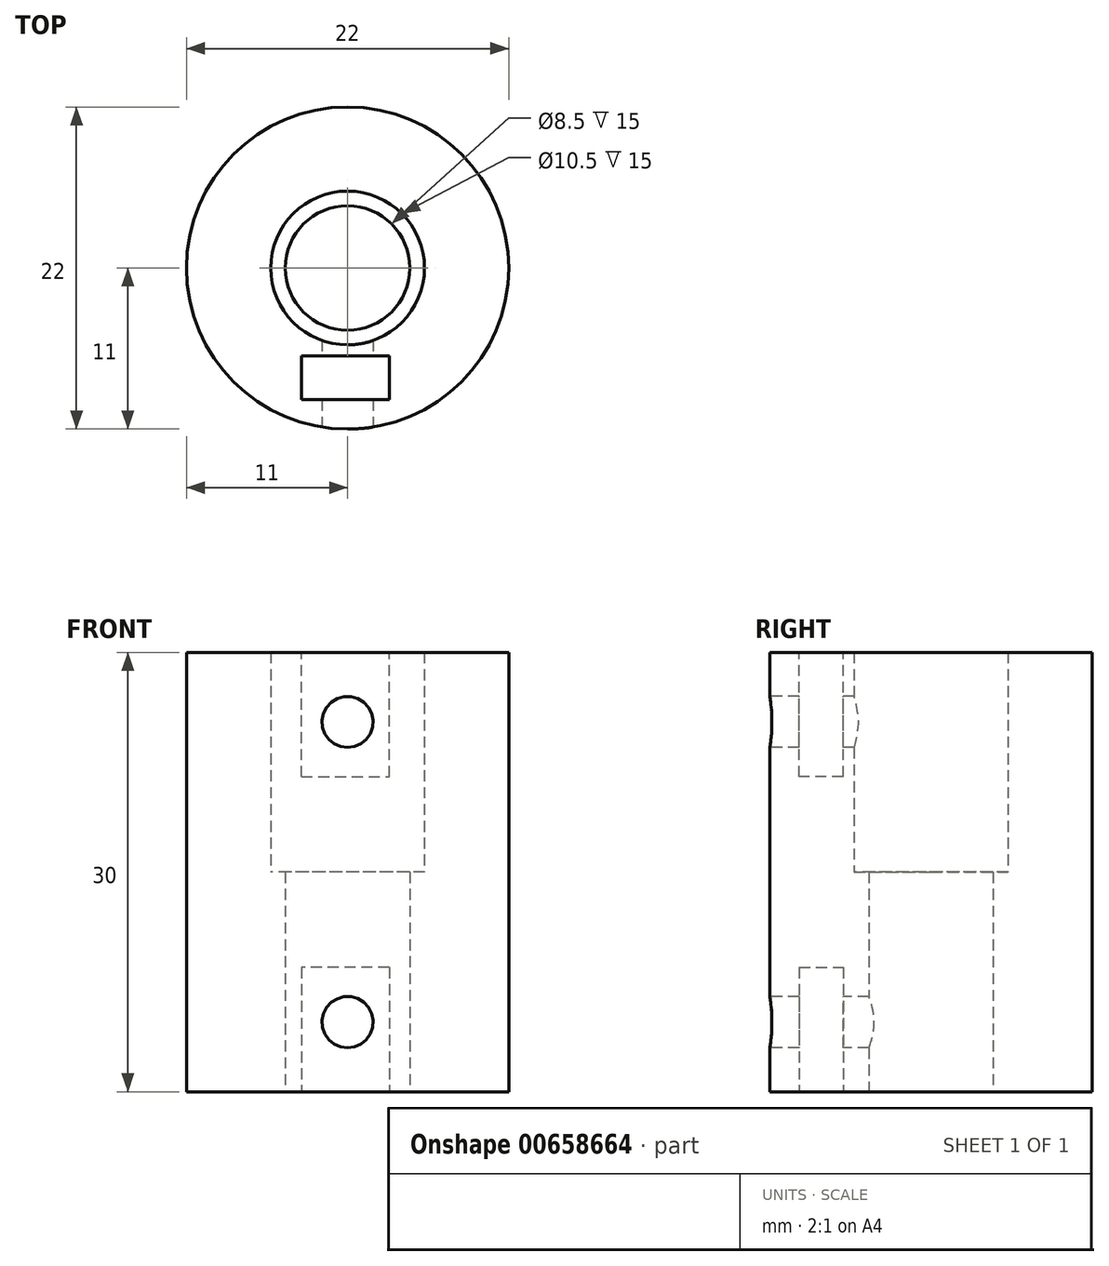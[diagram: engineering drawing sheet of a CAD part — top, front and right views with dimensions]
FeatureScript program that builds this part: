
annotation { "Feature Type Name" : "Feature", "Feature Type Description" : "" }
export const myFeature = defineFeature(function(context is Context, id is Id, definition is map)
    precondition{}
    {
        {
            var Q0;
            Q0=qCreatedBy(makeId("Top.planeOp"),FACE);
            var sketch = newSketch(context, id + "F0", { "sketchPlane" : qUnion([Q0])});
            skCircle(sketch, "E0", {"center": v(0, 0) * mm, "radius": 11 * mm});
            skCircle(sketch, "E1", {"center": v(0, 0) * mm, "radius": 4.25 * mm});
            skSolve(sketch);
        }
        {
            var Q0;
            Q0=makeQuery(id+"F0.imprint","IMPRINT",FACE,{"disambiguationData":[TD([[makeQuery(id+"F0.imprint","IMPRINT",EDGE,{"derivedFrom":sQuery(id+"F0.wireOp",EDGE,"E0")}),1.0]])]});
            extrude(context, id + "F1", {"entities" : qUnion([Q0]), "depth" : 15 * mm});
        }
        {
            var Q0;
            Q0=makeQuery(id+"F1.opExtrude","CAP_FACE",FACE,{"disambiguationData":[OSD([sQuery(id+"F0.wireOp",EDGE,"E0"),sQuery(id+"F0.wireOp",EDGE,"E1")])],"isStart":false});
            var sketch = newSketch(context, id + "F2", { "sketchPlane" : qUnion([Q0])});
            skCircle(sketch, "E2", {"center": v(0, 0) * mm, "radius": 11 * mm});
            skCircle(sketch, "E3", {"center": v(0, 0) * mm, "radius": 5.25 * mm});
            skSolve(sketch);
        }
        {
            var Q0;
            Q0=makeQuery(id+"F2.imprint","IMPRINT",FACE,{"disambiguationData":[TD([[makeQuery(id+"F2.imprint","IMPRINT",EDGE,{"derivedFrom":sQuery(id+"F2.wireOp",EDGE,"E2")}),1.0]])]});
            extrude(context, id + "F3", {"entities" : qUnion([Q0]), "operationType" : NewBodyOperationType.ADD, "depth" : 15 * mm});
        }
        {
            var Q0;
            Q0=makeQuery(id+"F3.opExtrude","CAP_FACE",FACE,{"disambiguationData":[OSD([sQuery(id+"F2.wireOp",EDGE,"E2"),sQuery(id+"F2.wireOp",EDGE,"E3")])],"isStart":false});
            var sketch = newSketch(context, id + "F4", { "sketchPlane" : qUnion([Q0])});
            skLineSegment(sketch, "E4.bottom", {"start": v(-3.15, -6) * mm, "end": v(2.85, -6) * mm});
            skLineSegment(sketch, "E4.top", {"start": v(-3.15, -9) * mm, "end": v(2.85, -9) * mm});
            skLineSegment(sketch, "E4.left", {"start": v(-3.15, -6) * mm, "end": v(-3.15, -9) * mm});
            skLineSegment(sketch, "E4.right", {"start": v(2.85, -6) * mm, "end": v(2.85, -9) * mm});
            skSolve(sketch);
        }
        {
            var Q0;
            Q0=makeQuery(id+"F4.imprint","IMPRINT",FACE,{"disambiguationData":[TD([[makeQuery(id+"F4.imprint","IMPRINT",EDGE,{"derivedFrom":sQuery(id+"F4.wireOp",EDGE,"E4.bottom")}),-1.0]])]});
            extrude(context, id + "F5", {"entities" : qUnion([Q0]), "operationType" : NewBodyOperationType.REMOVE, "oppositeDirection" : true, "depth" : 8.5 * mm});
        }
        {
            var Q0;
            Q0=makeQuery(id+"F5.boolean.opBoolean","COPY",FACE,{"derivedFrom":makeQuery(id+"F5.opExtrude","SWEPT_FACE",FACE,{"disambiguationData":[OSD([sQuery(id+"F4.wireOp",EDGE,"E4.bottom")])]})});
            var sketch = newSketch(context, id + "F6", { "sketchPlane" : qUnion([Q0])});
            skCircle(sketch, "E5", {"center": v(0, 25.25) * mm, "radius": 1.75 * mm});
            skLineSegment(sketch, "E6.0.0", {"start": v(2.85, 30) * mm, "end": v(-3.15, 30) * mm});
            skLineSegment(sketch, "E6.0.1", {"start": v(-3.15, 30) * mm, "end": v(-3.15, 21.5) * mm});
            skLineSegment(sketch, "E6.0.2", {"start": v(-3.15, 21.5) * mm, "end": v(2.85, 21.5) * mm});
            skLineSegment(sketch, "E6.0.3", {"start": v(2.85, 21.5) * mm, "end": v(2.85, 30) * mm});
            skSolve(sketch);
        }
        {
            var Q0;
            Q0=makeQuery(id+"F6.imprint","IMPRINT",FACE,{"disambiguationData":[TD([[makeQuery(id+"F6.imprint","IMPRINT",EDGE,{"derivedFrom":sQuery(id+"F6.wireOp",EDGE,"E5")}),1.0]])]});
            extrude(context, id + "F7", {"entities" : qUnion([Q0]), "operationType" : NewBodyOperationType.REMOVE, "oppositeDirection" : true, "depth" : 10 * mm, "symmetric" : true});
        }
        {
            var Q0;
            Q0=makeQuery(id+"F1.opExtrude","CAP_FACE",FACE,{"disambiguationData":[OSD([sQuery(id+"F0.wireOp",EDGE,"E0"),sQuery(id+"F0.wireOp",EDGE,"E1")])],"isStart":true});
            var sketch = newSketch(context, id + "F8", { "sketchPlane" : qUnion([Q0])});
            skCircle(sketch, "E7.0.0", {"center": v(0, 0) * mm, "radius": 11 * mm});
            skLineSegment(sketch, "E8.0.0", {"start": v(2.85, 6) * mm, "end": v(-3.15, 6) * mm});
            skLineSegment(sketch, "E8.0.1", {"start": v(-3.15, 6) * mm, "end": v(-3.15, 9) * mm});
            skLineSegment(sketch, "E8.0.2", {"start": v(-3.15, 9) * mm, "end": v(2.85, 9) * mm});
            skLineSegment(sketch, "E8.0.3", {"start": v(2.85, 9) * mm, "end": v(2.85, 6) * mm});
            skSolve(sketch);
        }
        {
            var Q0;
            Q0=makeQuery(id+"F8.imprint","IMPRINT",FACE,{"disambiguationData":[TD([[makeQuery(id+"F8.imprint","IMPRINT",EDGE,{"derivedFrom":sQuery(id+"F8.wireOp",EDGE,"E8.0.0")}),-1.0]])]});
            extrude(context, id + "F9", {"entities" : qUnion([Q0]), "operationType" : NewBodyOperationType.REMOVE, "oppositeDirection" : true, "depth" : 8.5 * mm});
        }
        {
            var Q0;
            Q0=makeQuery(id+"F9.boolean.opBoolean","COPY",FACE,{"derivedFrom":makeQuery(id+"F9.opExtrude","SWEPT_FACE",FACE,{"disambiguationData":[OSD([sQuery(id+"F8.wireOp",EDGE,"E8.0.0")])]})});
            var sketch = newSketch(context, id + "F10", { "sketchPlane" : qUnion([Q0])});
            skLineSegment(sketch, "E9.0.0", {"start": v(-3.15, 0) * mm, "end": v(2.85, 0) * mm});
            skLineSegment(sketch, "E9.0.1", {"start": v(2.85, 0) * mm, "end": v(2.85, 8.5) * mm});
            skLineSegment(sketch, "E9.0.2", {"start": v(2.85, 8.5) * mm, "end": v(-3.15, 8.5) * mm});
            skLineSegment(sketch, "E9.0.3", {"start": v(-3.15, 8.5) * mm, "end": v(-3.15, 0) * mm});
            skCircle(sketch, "E10", {"center": v(0, 4.75) * mm, "radius": 1.75 * mm});
            skSolve(sketch);
        }
        {
            var Q0;
            Q0=makeQuery(id+"F10.imprint","IMPRINT",FACE,{"disambiguationData":[TD([[makeQuery(id+"F10.imprint","IMPRINT",EDGE,{"derivedFrom":sQuery(id+"F10.wireOp",EDGE,"E10")}),1.0]])]});
            extrude(context, id + "F11", {"entities" : qUnion([Q0]), "operationType" : NewBodyOperationType.REMOVE, "oppositeDirection" : true, "depth" : 10 * mm, "symmetric" : true});
        }
    });
